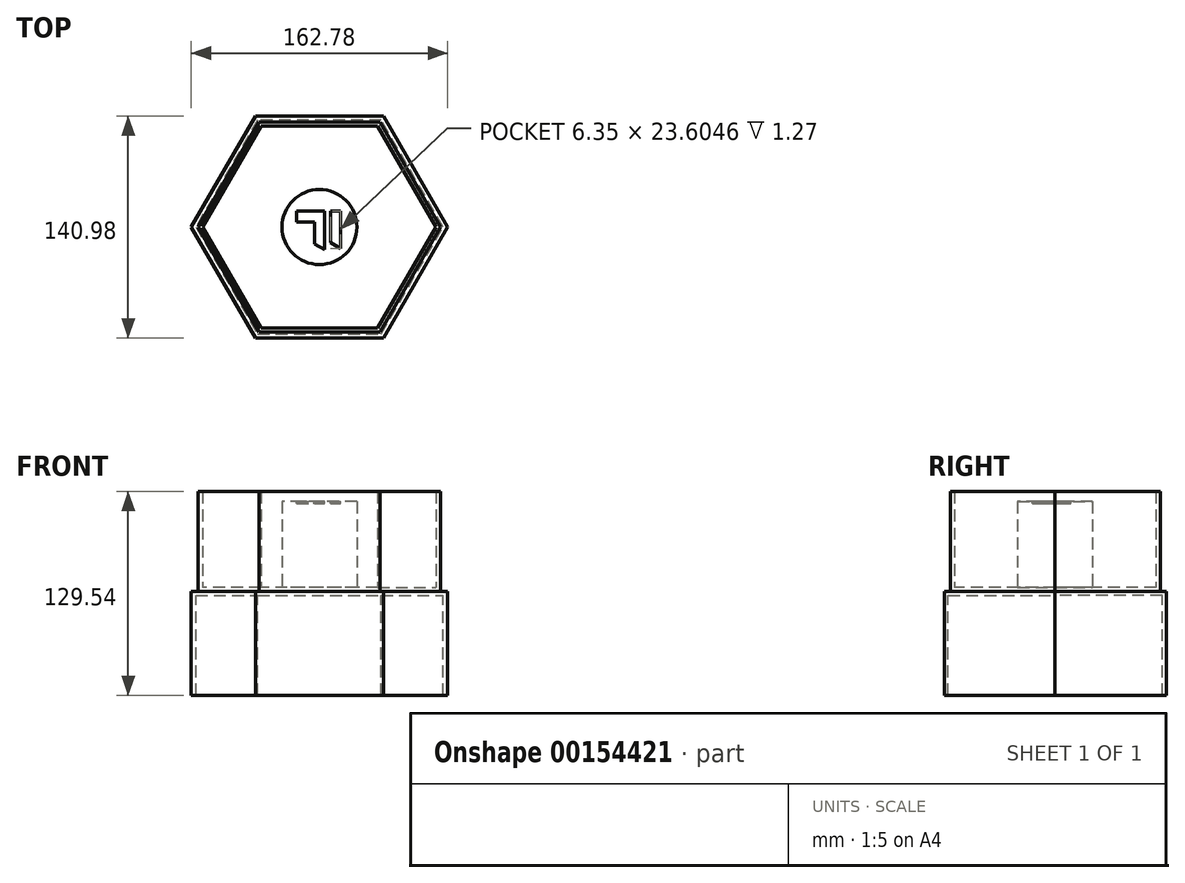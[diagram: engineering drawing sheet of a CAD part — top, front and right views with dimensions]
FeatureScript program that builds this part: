
annotation { "Feature Type Name" : "Feature", "Feature Type Description" : "" }
export const myFeature = defineFeature(function(context is Context, id is Id, definition is map)
    precondition{}
    {
        {
            var Q0;
            Q0=qCreatedBy(makeId("Top.planeOp"),FACE);
            var sketch = newSketch(context, id + "F0", { "sketchPlane" : qUnion([Q0])});
            skLineSegment(sketch, "E0", {"start": v(-38.5, 66.68) * mm, "end": v(38.5, 66.68) * mm});
            skLineSegment(sketch, "E1", {"start": v(38.5, 66.68) * mm, "end": v(76.99, 0) * mm});
            skLineSegment(sketch, "E2", {"start": v(76.99, 0) * mm, "end": v(38.5, -66.68) * mm});
            skLineSegment(sketch, "E3", {"start": v(38.5, -66.68) * mm, "end": v(-38.5, -66.68) * mm});
            skLineSegment(sketch, "E4", {"start": v(-38.5, -66.68) * mm, "end": v(-76.99, 0) * mm});
            skLineSegment(sketch, "E5", {"start": v(-76.99, 0) * mm, "end": v(-38.5, 66.68) * mm});
            skLineSegment(sketch, "E6", {"start": v(0, 66.68) * mm, "end": v(0, -66.68) * mm, "construction": true});
            skCircle(sketch, "E7", {"center": v(0, 0) * mm, "radius": 23.81 * mm});
            skLineSegment(sketch, "E8.0", {"start": v(37.03, 64.14) * mm, "end": v(74.06, 0) * mm});
            skLineSegment(sketch, "E8.1", {"start": v(37.03, -64.14) * mm, "end": v(-37.03, -64.14) * mm});
            skLineSegment(sketch, "E8.2", {"start": v(-37.03, -64.14) * mm, "end": v(-74.06, 0) * mm});
            skLineSegment(sketch, "E8.3", {"start": v(74.06, 0) * mm, "end": v(37.03, -64.14) * mm});
            skLineSegment(sketch, "E8.4", {"start": v(-74.06, 0) * mm, "end": v(-37.03, 64.14) * mm});
            skLineSegment(sketch, "E8.5", {"start": v(-37.03, 64.14) * mm, "end": v(37.03, 64.14) * mm});
            skLineSegment(sketch, "E9.0", {"start": v(78.46, 0) * mm, "end": v(39.23, -67.95) * mm});
            skLineSegment(sketch, "E9.1", {"start": v(-39.23, -67.95) * mm, "end": v(-78.46, 0) * mm});
            skLineSegment(sketch, "E9.2", {"start": v(-78.46, 0) * mm, "end": v(-39.23, 67.95) * mm});
            skLineSegment(sketch, "E9.3", {"start": v(39.23, -67.95) * mm, "end": v(-39.23, -67.95) * mm});
            skLineSegment(sketch, "E9.4", {"start": v(-39.23, 67.95) * mm, "end": v(39.23, 67.95) * mm});
            skLineSegment(sketch, "E9.5", {"start": v(39.23, 67.95) * mm, "end": v(78.46, 0) * mm});
            skLineSegment(sketch, "E10.0", {"start": v(81.39, 0) * mm, "end": v(40.7, -70.48) * mm});
            skLineSegment(sketch, "E10.1", {"start": v(-40.7, -70.48) * mm, "end": v(-81.39, 0) * mm});
            skLineSegment(sketch, "E10.2", {"start": v(-81.39, 0) * mm, "end": v(-40.7, 70.49) * mm});
            skLineSegment(sketch, "E10.3", {"start": v(40.7, -70.48) * mm, "end": v(-40.7, -70.48) * mm});
            skLineSegment(sketch, "E10.4", {"start": v(-40.7, 70.48) * mm, "end": v(40.7, 70.48) * mm});
            skLineSegment(sketch, "E10.5", {"start": v(40.7, 70.49) * mm, "end": v(81.39, 0) * mm});
            skSolve(sketch);
        }
        {
            var Q0;
            Q0=makeQuery(id+"F0.imprint","IMPRINT",FACE,{"disambiguationData":[TD([[makeQuery(id+"F0.imprint","IMPRINT",EDGE,{"derivedFrom":sQuery(id+"F0.wireOp",EDGE,"E0")}),-1.0]])]});
            extrude(context, id + "F1", {"entities" : qUnion([Q0]), "depth" : 63.5 * mm});
        }
        {
            var Q0;
            Q0=makeQuery(id+"F0.imprint","IMPRINT",FACE,{"disambiguationData":[TD([[makeQuery(id+"F0.imprint","IMPRINT",EDGE,{"derivedFrom":sQuery(id+"F0.wireOp",EDGE,"E7")}),-1.0]])]});
            extrude(context, id + "F2", {"entities" : qUnion([Q0]), "operationType" : NewBodyOperationType.ADD, "depth" : 2.54 * mm});
        }
        {
            var Q0;
            Q0=makeQuery(id+"F0.imprint","IMPRINT",FACE,{"disambiguationData":[TD([[makeQuery(id+"F0.imprint","IMPRINT",EDGE,{"derivedFrom":sQuery(id+"F0.wireOp",EDGE,"E7")}),1.0]])]});
            extrude(context, id + "F3", {"entities" : qUnion([Q0]), "operationType" : NewBodyOperationType.ADD, "depth" : 57.15 * mm});
        }
        {
            var Q0;
            Q0=makeQuery(id+"F0.imprint","IMPRINT",FACE,{"disambiguationData":[TD([[makeQuery(id+"F0.imprint","IMPRINT",EDGE,{"derivedFrom":sQuery(id+"F0.wireOp",EDGE,"E9.0")}),1.0]])]});
            extrude(context, id + "F4", {"entities" : qUnion([Q0]), "oppositeDirection" : true, "depth" : 66.04 * mm});
        }
        {
            var Q0;
            Q0=makeQuery(id+"F0.imprint","IMPRINT",FACE,{"disambiguationData":[TD([[makeQuery(id+"F0.imprint","IMPRINT",EDGE,{"derivedFrom":sQuery(id+"F0.wireOp",EDGE,"E9.0")}),1.0]])]});
            var Q1;
            Q1=makeQuery(id+"F0.imprint","IMPRINT",FACE,{"disambiguationData":[TD([[makeQuery(id+"F0.imprint","IMPRINT",EDGE,{"derivedFrom":sQuery(id+"F0.wireOp",EDGE,"E0")}),1.0]])]});
            var Q2;
            Q2=makeQuery(id+"F0.imprint","IMPRINT",FACE,{"disambiguationData":[TD([[makeQuery(id+"F0.imprint","IMPRINT",EDGE,{"derivedFrom":sQuery(id+"F0.wireOp",EDGE,"E0")}),-1.0]])]});
            var Q3;
            Q3=makeQuery(id+"F0.imprint","IMPRINT",FACE,{"disambiguationData":[TD([[makeQuery(id+"F0.imprint","IMPRINT",EDGE,{"derivedFrom":sQuery(id+"F0.wireOp",EDGE,"E7")}),1.0]])]});
            var Q4;
            Q4=makeQuery(id+"F0.imprint","IMPRINT",FACE,{"disambiguationData":[TD([[makeQuery(id+"F0.imprint","IMPRINT",EDGE,{"derivedFrom":sQuery(id+"F0.wireOp",EDGE,"E7")}),-1.0]])]});
            extrude(context, id + "F5", {"entities" : qUnion([Q0, Q1, Q2, Q3, Q4]), "operationType" : NewBodyOperationType.ADD, "oppositeDirection" : true, "depth" : 2.54 * mm});
        }
        {
            var Q0;
            Q0=makeQuery(id+"F3.opExtrude","CAP_FACE",FACE,{"disambiguationData":[OSD([sQuery(id+"F0.wireOp",EDGE,"E7")])],"isStart":false});
            var sketch = newSketch(context, id + "F6", { "sketchPlane" : qUnion([Q0])});
            skLineSegment(sketch, "E11", {"start": v(13.46, 10.08) * mm, "end": v(13.46, -13.52) * mm});
            skLineSegment(sketch, "E12", {"start": v(13.46, -13.52) * mm, "end": v(7.11, -9.86) * mm});
            skLineSegment(sketch, "E13", {"start": v(7.11, -9.86) * mm, "end": v(7.11, 10.08) * mm});
            skLineSegment(sketch, "E14", {"start": v(7.11, 10.08) * mm, "end": v(13.46, 10.08) * mm});
            skLineSegment(sketch, "E15", {"start": v(3.3, 10.08) * mm, "end": v(-14.48, 10.08) * mm});
            skLineSegment(sketch, "E16", {"start": v(-14.48, 10.08) * mm, "end": v(-14.48, 3.23) * mm});
            skLineSegment(sketch, "E17", {"start": v(-14.48, 3.23) * mm, "end": v(-3.05, 3.23) * mm});
            skLineSegment(sketch, "E18", {"start": v(-3.05, 3.23) * mm, "end": v(-3.05, -10.65) * mm});
            skLineSegment(sketch, "E19", {"start": v(-3.05, -10.65) * mm, "end": v(3.3, -14.31) * mm});
            skLineSegment(sketch, "E20", {"start": v(3.3, -14.31) * mm, "end": v(3.3, 10.08) * mm});
            skSolve(sketch);
        }
        {
            var Q0;
            Q0 = qSketchRegion(id + "F6", true);
            extrude(context, id + "F7", {"entities" : qUnion([Q0]), "operationType" : NewBodyOperationType.REMOVE, "oppositeDirection" : true, "depth" : 1.27 * mm});
        }
    });
